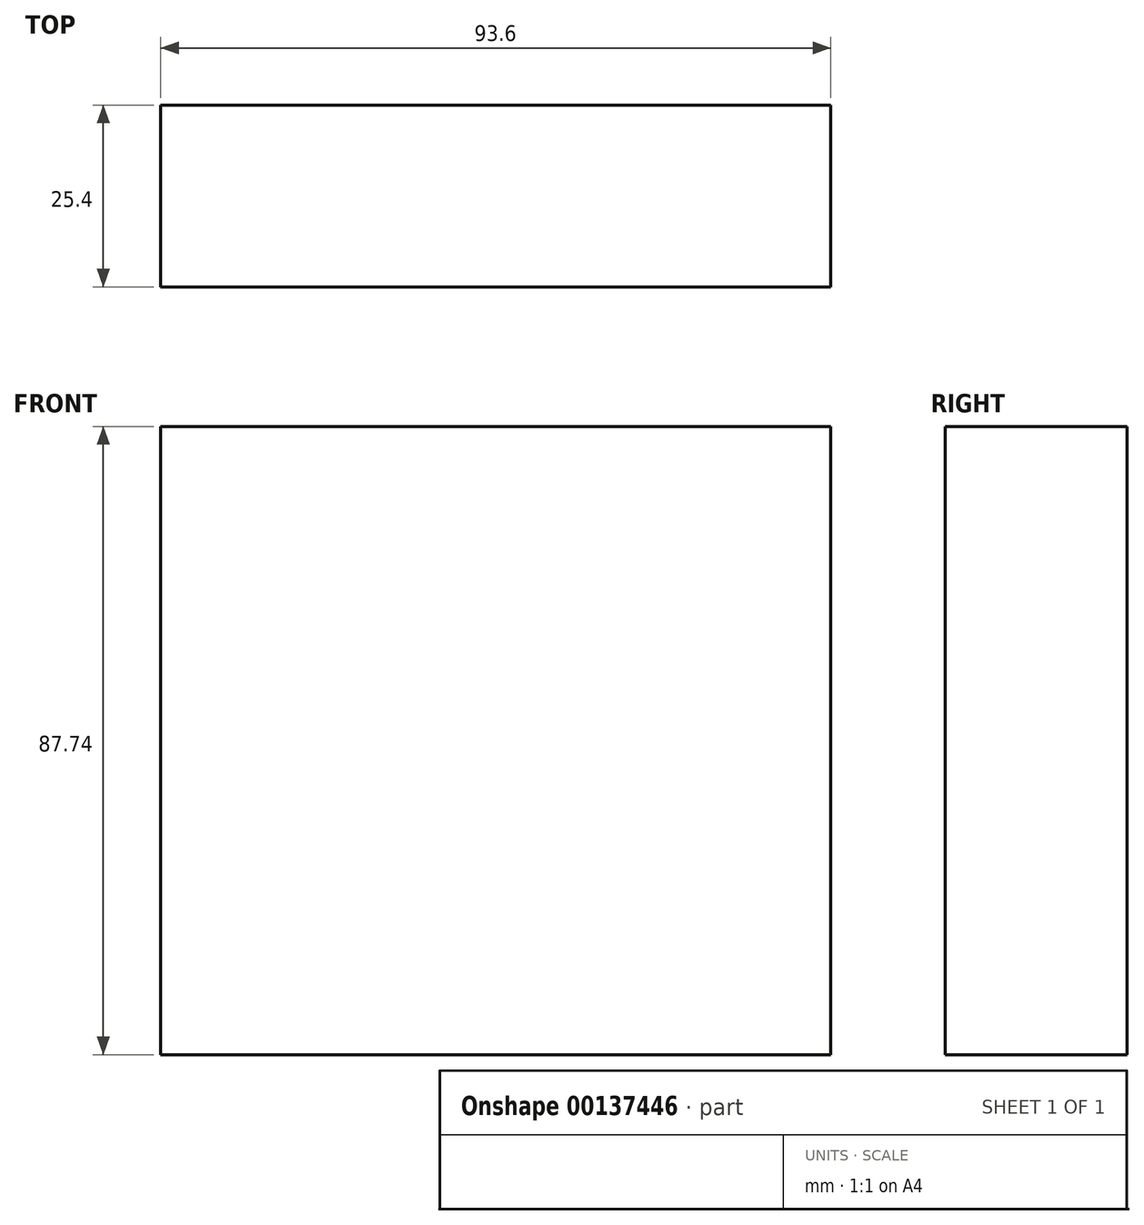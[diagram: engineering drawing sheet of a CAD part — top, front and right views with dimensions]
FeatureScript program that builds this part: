
annotation { "Feature Type Name" : "Feature", "Feature Type Description" : "" }
export const myFeature = defineFeature(function(context is Context, id is Id, definition is map)
    precondition{}
    {
        {
            var Q0;
            Q0=qCreatedBy(makeId("Front.planeOp"),FACE);
            var sketch = newSketch(context, id + "F2", { "sketchPlane" : qUnion([Q0])});
            skLineSegment(sketch, "E0.bottom", {"start": v(-47.9, 42.28) * mm, "end": v(45.7, 42.28) * mm});
            skLineSegment(sketch, "E0.top", {"start": v(-47.9, -45.46) * mm, "end": v(45.7, -45.46) * mm});
            skLineSegment(sketch, "E0.left", {"start": v(-47.9, 42.28) * mm, "end": v(-47.9, -45.46) * mm});
            skLineSegment(sketch, "E0.right", {"start": v(45.7, 42.28) * mm, "end": v(45.7, -45.46) * mm});
            skSolve(sketch);
        }
        {
            var Q0;
            Q0=makeQuery(id+"F2.imprint","IMPRINT",FACE,{"disambiguationData":[TD([[makeQuery(id+"F2.imprint","IMPRINT",EDGE,{"derivedFrom":sQuery(id+"F2.wireOp",EDGE,"E0.bottom")}),-1.0]])]});
            extrude(context, id + "F0", {"entities" : qUnion([Q0]), "depth" : 25.4 * mm});
        }
        {
            var Q0;
            Q0=qCreatedBy(makeId("Right.planeOp"),FACE);
            var sketch = newSketch(context, id + "F1", { "sketchPlane" : qUnion([Q0])});
            skLineSegment(sketch, "E1", {"start": v(0, 88.22) * mm, "end": v(0, -97.75) * mm, "construction": true});
            skSolve(sketch);
        }
    });
